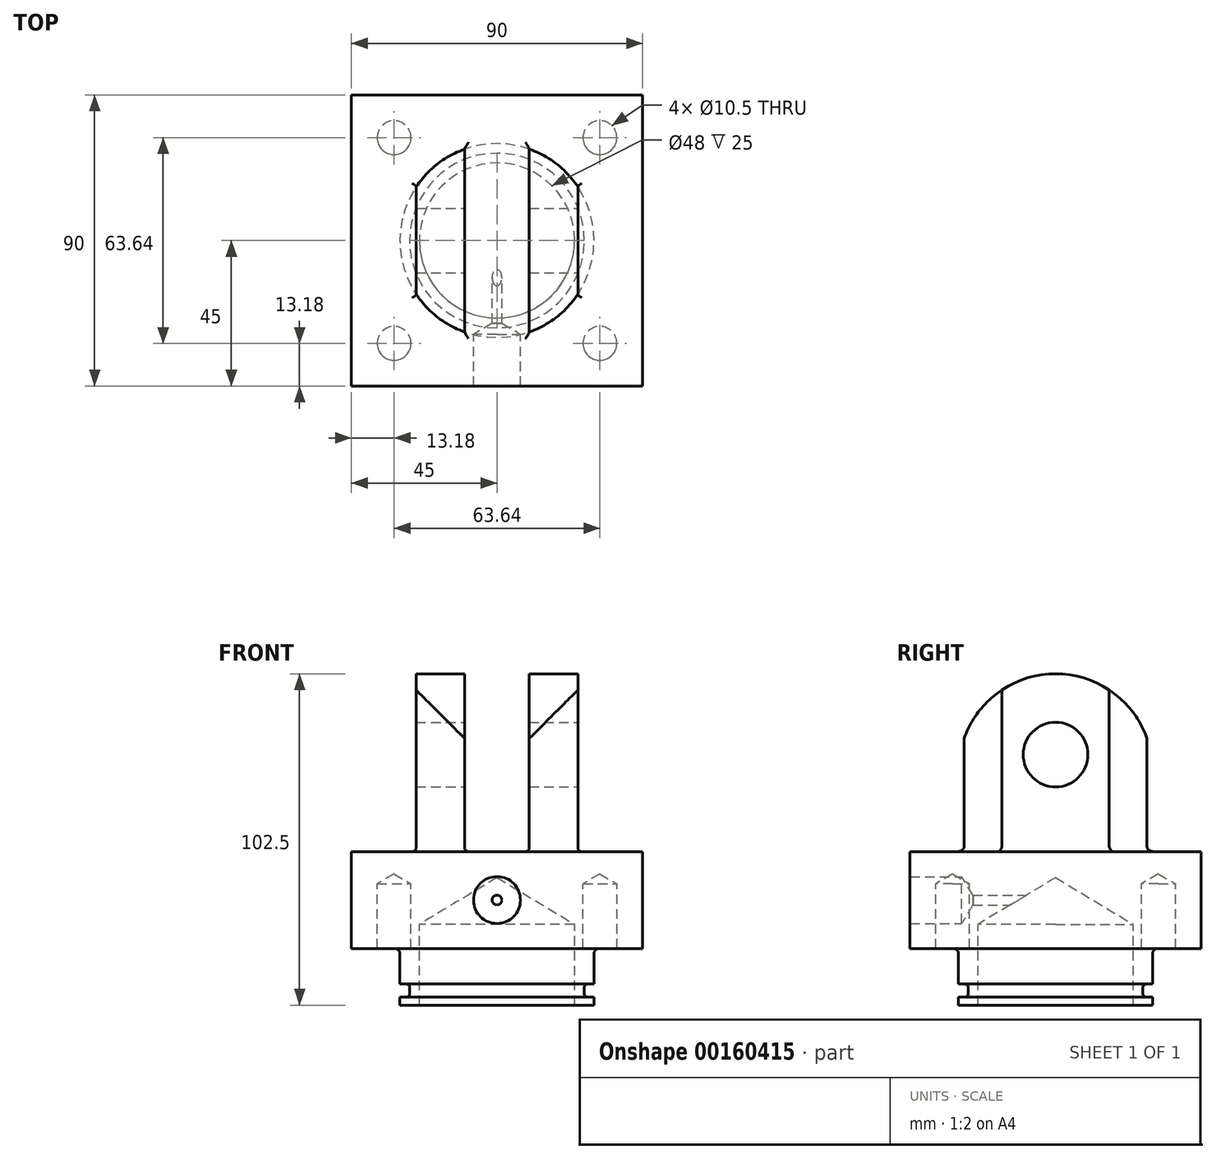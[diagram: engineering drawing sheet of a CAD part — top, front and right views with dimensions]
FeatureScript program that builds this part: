
annotation { "Feature Type Name" : "Feature", "Feature Type Description" : "" }
export const myFeature = defineFeature(function(context is Context, id is Id, definition is map)
    precondition{}
    {
        {
            var Q0;
            Q0=qCreatedBy(makeId("Top.planeOp"),FACE);
            var sketch = newSketch(context, id + "F0", { "sketchPlane" : qUnion([Q0])});
            skLineSegment(sketch, "E0.bottom", {"start": v(45, 45) * mm, "end": v(-45, 45) * mm});
            skLineSegment(sketch, "E0.top", {"start": v(45, -45) * mm, "end": v(-45, -45) * mm});
            skLineSegment(sketch, "E0.left", {"start": v(45, 45) * mm, "end": v(45, -45) * mm});
            skLineSegment(sketch, "E0.right", {"start": v(-45, 45) * mm, "end": v(-45, -45) * mm});
            skPoint(sketch, "E0.middle", {"position": v(0, 0) * mm});
            skSolve(sketch);
        }
        {
            var Q0;
            Q0 = qSketchRegion(id + "F0", true);
            extrude(context, id + "F1", {"entities" : qUnion([Q0]), "depth" : 102.5 * mm});
        }
        {
            var Q0;
            Q0=makeQuery(id+"F1.opExtrude","CAP_VERTEX",VERTEX,{"disambiguationData":[OSD([sQuery(id+"F0.wireOp",EDGE,"E0.top"),sQuery(id+"F0.wireOp",EDGE,"E0.right")])],"isStart":false});
            var Q1;
            Q1=makeQuery(id+"F1.opExtrude","CAP_VERTEX",VERTEX,{"disambiguationData":[OSD([sQuery(id+"F0.wireOp",EDGE,"E0.bottom"),sQuery(id+"F0.wireOp",EDGE,"E0.left")])],"isStart":false});
            var Q2;
            Q2=makeQuery(id+"F1.opExtrude","CAP_VERTEX",VERTEX,{"disambiguationData":[OSD([sQuery(id+"F0.wireOp",EDGE,"E0.bottom"),sQuery(id+"F0.wireOp",EDGE,"E0.left")])],"isStart":true});
            cPlane(context, id + "F2", {"entities" : qUnion([Q0, Q1, Q2]), "cplaneType" : CPlaneType.THREE_POINT, "offset" : 25 * mm, "width" : 150 * mm, "height" : 150 * mm});
        }
        {
            var Q0;
            Q0=qCreatedBy(id+"F2.planeOp",FACE);
            var sketch = newSketch(context, id + "F3", { "sketchPlane" : qUnion([Q0])});
            skLineSegment(sketch, "E1.bottom", {"start": v(-63.64, 102.5) * mm, "end": v(-30, 102.5) * mm});
            skLineSegment(sketch, "E1.top", {"start": v(-63.64, 47.5) * mm, "end": v(-31.6, 47.5) * mm});
            skLineSegment(sketch, "E1.left", {"start": v(-63.64, 102.5) * mm, "end": v(-63.64, 47.5) * mm});
            skLineSegment(sketch, "E1.right", {"start": v(-30, 102.5) * mm, "end": v(-30, 49.1) * mm});
            skLineSegment(sketch, "E2.bottom", {"start": v(-63.64, 0) * mm, "end": v(-30, 0) * mm});
            skLineSegment(sketch, "E2.top", {"start": v(-63.64, 17.5) * mm, "end": v(-31.6, 17.5) * mm});
            skLineSegment(sketch, "E2.left", {"start": v(-63.64, 0) * mm, "end": v(-63.64, 17.5) * mm});
            skLineSegment(sketch, "E2.right", {"start": v(-30, 0) * mm, "end": v(-30, 2.5) * mm});
            skLineSegment(sketch, "E3", {"start": v(0, -1.6) * mm, "end": v(0, 125.64) * mm, "construction": true});
            skLineSegment(sketch, "E4.bottom", {"start": v(-30, 2.5) * mm, "end": v(-28, 2.5) * mm});
            skLineSegment(sketch, "E4.top", {"start": v(-30, 6.5) * mm, "end": v(-28, 6.5) * mm});
            skLineSegment(sketch, "E4.right", {"start": v(-27, 3.5) * mm, "end": v(-27, 5.5) * mm});
            skLineSegment(sketch, "E5.trimOffspring", {"start": v(-30, 6.5) * mm, "end": v(-30, 15.9) * mm});
            skPoint(sketch, "E6.visualSharp", {"position": v(-30, 47.5) * mm});
            skArc(sketch, "E6.filletArc", {"start": v(-31.6, 47.5) * mm, "mid": v(-30.47, 47.97) * mm, "end": v(-30, 49.1) * mm});
            skPoint(sketch, "E7.visualSharp", {"position": v(-30, 17.5) * mm});
            skArc(sketch, "E7.filletArc", {"start": v(-30, 15.9) * mm, "mid": v(-30.47, 17.03) * mm, "end": v(-31.6, 17.5) * mm});
            skPoint(sketch, "E8.visualSharp", {"position": v(-27, 6.5) * mm});
            skArc(sketch, "E8.filletArc", {"start": v(-27, 5.5) * mm, "mid": v(-27.3, 6.2) * mm, "end": v(-28, 6.5) * mm});
            skPoint(sketch, "E9.visualSharp", {"position": v(-27, 2.5) * mm});
            skArc(sketch, "E9.filletArc", {"start": v(-28, 2.5) * mm, "mid": v(-27.3, 2.8) * mm, "end": v(-27, 3.5) * mm});
            skSolve(sketch);
        }
        {
            var Q0;
            Q0 = qSketchRegion(id + "F3", true);
            var Q1;
            Q1=sQuery(id+"F3.wireOp",EDGE,"E3");
            revolve(context, id + "F4", {"operationType" : NewBodyOperationType.REMOVE, "entities" : qUnion([Q0]), "axis" : qUnion([Q1]), "revolveType" : RevolveType.FULL, "oppositeDirection" : true});
        }
        {
            var Q0;
            Q0=makeQuery(id+"F1.opExtrude","CAP_FACE",FACE,{"disambiguationData":[OSD([sQuery(id+"F0.wireOp",EDGE,"E0.bottom"),sQuery(id+"F0.wireOp",EDGE,"E0.top"),sQuery(id+"F0.wireOp",EDGE,"E0.left"),sQuery(id+"F0.wireOp",EDGE,"E0.right")])],"isStart":true});
            var sketch = newSketch(context, id + "F5", { "sketchPlane" : qUnion([Q0])});
            skPoint(sketch, "E10", {"position": v(0, 0) * mm});
            skSolve(sketch);
        }
        {
            var Q0;
            Q0=sQuery(id+"F5.wireOp",VERTEX,"E10");
            var Q1;
            Q1=makeQuery(id+"F1.opExtrude","SWEPT_BODY",BODY,{"disambiguationData":[OSD([sQuery(id+"F0.wireOp",EDGE,"E0.bottom"),sQuery(id+"F0.wireOp",EDGE,"E0.top"),sQuery(id+"F0.wireOp",EDGE,"E0.left"),sQuery(id+"F0.wireOp",EDGE,"E0.right")])]});
            hole(context, id + "F6", {"style" : HoleStyle.SIMPLE, "endStyle" : HoleEndStyle.BLIND, "holeDiameter" : 48 * mm, "holeDepth" : 25 * mm, "locations" : qUnion([Q0]), "scope" : qUnion([Q1]), "startStyle" : HoleStartStyle.SKETCH});
        }
        {
            var Q0;
            Q0=qCreatedBy(makeId("Front.planeOp"),FACE);
            var sketch = newSketch(context, id + "F7", { "sketchPlane" : qUnion([Q0])});
            skLineSegment(sketch, "E11.bottom", {"start": v(-45, 47.5) * mm, "end": v(-26.2, 47.5) * mm});
            skLineSegment(sketch, "E11.top", {"start": v(-45, 102.5) * mm, "end": v(-25, 102.5) * mm});
            skLineSegment(sketch, "E11.left", {"start": v(-45, 47.5) * mm, "end": v(-45, 102.5) * mm});
            skLineSegment(sketch, "E11.right", {"start": v(-25, 48.7) * mm, "end": v(-25, 102.5) * mm});
            skLineSegment(sketch, "E12.bottom", {"start": v(8.8, 47.5) * mm, "end": v(-8.8, 47.5) * mm});
            skLineSegment(sketch, "E12.top", {"start": v(10, 102.5) * mm, "end": v(-10, 102.5) * mm});
            skLineSegment(sketch, "E12.left", {"start": v(10, 48.7) * mm, "end": v(10, 102.5) * mm});
            skLineSegment(sketch, "E12.right", {"start": v(-10, 48.7) * mm, "end": v(-10, 102.5) * mm});
            skLineSegment(sketch, "E13.bottom", {"start": v(45, 47.5) * mm, "end": v(26.2, 47.5) * mm});
            skLineSegment(sketch, "E13.top", {"start": v(45, 102.5) * mm, "end": v(25, 102.5) * mm});
            skLineSegment(sketch, "E13.left", {"start": v(45, 47.5) * mm, "end": v(45, 102.5) * mm});
            skLineSegment(sketch, "E13.right", {"start": v(25, 48.7) * mm, "end": v(25, 102.5) * mm});
            skLineSegment(sketch, "E14", {"start": v(0, -1.6) * mm, "end": v(0, 109.32) * mm, "construction": true});
            skPoint(sketch, "E15.visualSharp", {"position": v(-25, 47.5) * mm});
            skArc(sketch, "E15.filletArc", {"start": v(-26.2, 47.5) * mm, "mid": v(-25.35, 47.85) * mm, "end": v(-25, 48.7) * mm});
            skPoint(sketch, "E16.visualSharp", {"position": v(-10, 47.5) * mm});
            skArc(sketch, "E16.filletArc", {"start": v(-10, 48.7) * mm, "mid": v(-9.65, 47.85) * mm, "end": v(-8.8, 47.5) * mm});
            skPoint(sketch, "E17.visualSharp", {"position": v(10, 47.5) * mm});
            skArc(sketch, "E17.filletArc", {"start": v(8.8, 47.5) * mm, "mid": v(9.65, 47.85) * mm, "end": v(10, 48.7) * mm});
            skPoint(sketch, "E18.visualSharp", {"position": v(25, 47.5) * mm});
            skArc(sketch, "E18.filletArc", {"start": v(25, 48.7) * mm, "mid": v(25.35, 47.85) * mm, "end": v(26.2, 47.5) * mm});
            skSolve(sketch);
        }
        {
            var Q0;
            Q0 = qSketchRegion(id + "F7", true);
            extrude(context, id + "F8", {"entities" : qUnion([Q0]), "operationType" : NewBodyOperationType.REMOVE, "endBound" : BoundingType.THROUGH_ALL, "oppositeDirection" : true, "depth" : 25 * mm, "hasSecondDirection" : true, "secondDirectionBound" : BoundingType.THROUGH_ALL, "secondDirectionOppositeDirection" : false, "secondDirectionDepth" : 25 * mm});
        }
        {
            var Q0;
            Q0=qCreatedBy(makeId("Right.planeOp"),FACE);
            var sketch = newSketch(context, id + "F9", { "sketchPlane" : qUnion([Q0])});
            skArc(sketch, "E19", {"start": v(28.28, 82.5) * mm, "mid": v(0, 102.5) * mm, "end": v(-28.28, 82.5) * mm});
            skLineSegment(sketch, "E20", {"start": v(28.28, 82.5) * mm, "end": v(28.28, 102.5) * mm});
            skLineSegment(sketch, "E21", {"start": v(28.28, 102.5) * mm, "end": v(-28.28, 102.5) * mm});
            skLineSegment(sketch, "E22", {"start": v(-28.28, 102.5) * mm, "end": v(-28.28, 82.5) * mm});
            skCircle(sketch, "E23", {"center": v(0, 77.5) * mm, "radius": 10 * mm});
            skSolve(sketch);
        }
        {
            var Q0;
            Q0 = qSketchRegion(id + "F9", true);
            var Q1;
            Q1=makeQuery(id+"F8.boolean.opBoolean","COPY",FACE,{"derivedFrom":makeQuery(id+"F8.opExtrude","SWEPT_FACE",FACE,{"disambiguationData":[OSD([sQuery(id+"F7.wireOp",EDGE,"E11.right")])]})});
            var Q2;
            Q2=makeQuery(id+"F8.boolean.opBoolean","COPY",FACE,{"derivedFrom":makeQuery(id+"F8.opExtrude","SWEPT_FACE",FACE,{"disambiguationData":[OSD([sQuery(id+"F7.wireOp",EDGE,"E13.right")])]})});
            extrude(context, id + "F10", {"entities" : qUnion([Q0]), "operationType" : NewBodyOperationType.REMOVE, "endBound" : BoundingType.UP_TO_SURFACE, "oppositeDirection" : true, "endBoundEntityFace" : qUnion([Q1]), "depth" : 25 * mm, "hasSecondDirection" : true, "secondDirectionBound" : BoundingType.UP_TO_SURFACE, "secondDirectionOppositeDirection" : false, "secondDirectionBoundEntityFace" : qUnion([Q2]), "secondDirectionDepth" : 25 * mm});
        }
        {
            var Q0;
            Q0=makeQuery(id+"F4.boolean.opBoolean","COPY",FACE,{"derivedFrom":makeQuery(id+"F4.opRevolve","SWEPT_FACE",FACE,{"disambiguationData":[OSD([sQuery(id+"F3.wireOp",EDGE,"E2.top")])]})});
            var sketch = newSketch(context, id + "F11", { "sketchPlane" : qUnion([Q0])});
            skLineSegment(sketch, "E24", {"start": v(45, -45) * mm, "end": v(-45, 45) * mm, "construction": true});
            skLineSegment(sketch, "E25", {"start": v(45, 45) * mm, "end": v(-45, -45) * mm, "construction": true});
            skCircle(sketch, "E26", {"center": v(0, 0) * mm, "radius": 45 * mm, "construction": true});
            skPoint(sketch, "E27", {"position": v(-31.82, -31.82) * mm});
            skPoint(sketch, "E28", {"position": v(-31.82, 31.82) * mm});
            skPoint(sketch, "E29", {"position": v(31.82, 31.82) * mm});
            skPoint(sketch, "E30", {"position": v(31.82, -31.82) * mm});
            skSolve(sketch);
        }
        {
            var Q0;
            Q0=sQuery(id+"F11.wireOp",VERTEX,"E27");
            var Q1;
            Q1=sQuery(id+"F11.wireOp",VERTEX,"E28");
            var Q2;
            Q2=sQuery(id+"F11.wireOp",VERTEX,"E29");
            var Q3;
            Q3=sQuery(id+"F11.wireOp",VERTEX,"E30");
            var Q4;
            Q4=makeQuery(id+"F1.opExtrude","SWEPT_BODY",BODY,{"disambiguationData":[OSD([sQuery(id+"F0.wireOp",EDGE,"E0.bottom"),sQuery(id+"F0.wireOp",EDGE,"E0.top"),sQuery(id+"F0.wireOp",EDGE,"E0.left"),sQuery(id+"F0.wireOp",EDGE,"E0.right")])]});
            hole(context, id + "F12", {"style" : HoleStyle.SIMPLE, "endStyle" : HoleEndStyle.BLIND, "standardTappedOrClearance" : lookupTablePath({ "standard" : "ISO", "engagement" : "75%", "pitch" : "1.5 mm", "size" : "M12", "type" : "Tapped" }), "standardBlindInLast" : lookupTablePath({ "standard" : "ISO", "engagement" : "75%", "pitch" : "1.5 mm", "size" : "M12", "type" : "Tapped" }), "holeDiameter" : 10.5 * mm, "holeDepth" : 20 * mm, "locations" : qUnion([Q0, Q1, Q2, Q3]), "scope" : qUnion([Q4]), "tappedDepth" : 12 * mm, "tapClearance" : 3, "majorDiameter" : 12 * mm, "startStyle" : HoleStartStyle.SKETCH});
        }
        {
            var Q0;
            Q0=makeQuery(id+"F1.opExtrude","SWEPT_FACE",FACE,{"disambiguationData":[OSD([sQuery(id+"F0.wireOp",EDGE,"E0.top")])]});
            var sketch = newSketch(context, id + "F13", { "sketchPlane" : qUnion([Q0])});
            skPoint(sketch, "E31", {"position": v(0, 32.5) * mm});
            skSolve(sketch);
        }
        {
            var Q0;
            Q0=sQuery(id+"F13.wireOp",VERTEX,"E31");
            var Q1;
            Q1=makeQuery(id+"F1.opExtrude","SWEPT_BODY",BODY,{"disambiguationData":[OSD([sQuery(id+"F0.wireOp",EDGE,"E0.bottom"),sQuery(id+"F0.wireOp",EDGE,"E0.top"),sQuery(id+"F0.wireOp",EDGE,"E0.left"),sQuery(id+"F0.wireOp",EDGE,"E0.right")])]});
            hole(context, id + "F14", {"style" : HoleStyle.SIMPLE, "endStyle" : HoleEndStyle.BLIND, "holeDiameter" : 3 * mm, "holeDepth" : 45 * mm, "locations" : qUnion([Q0]), "scope" : qUnion([Q1]), "startStyle" : HoleStartStyle.SKETCH});
        }
        {
            var Q0;
            Q0=sQuery(id+"F13.wireOp",VERTEX,"E31");
            var Q1;
            Q1=makeQuery(id+"F1.opExtrude","SWEPT_BODY",BODY,{"disambiguationData":[OSD([sQuery(id+"F0.wireOp",EDGE,"E0.bottom"),sQuery(id+"F0.wireOp",EDGE,"E0.top"),sQuery(id+"F0.wireOp",EDGE,"E0.left"),sQuery(id+"F0.wireOp",EDGE,"E0.right")])]});
            hole(context, id + "F15", {"style" : HoleStyle.SIMPLE, "endStyle" : HoleEndStyle.BLIND, "standardTappedOrClearance" : lookupTablePath({ "standard" : "ISO", "engagement" : "75%", "pitch" : "1.5 mm", "size" : "M16", "type" : "Tapped" }), "standardBlindInLast" : lookupTablePath({ "standard" : "ISO", "engagement" : "75%", "pitch" : "1.5 mm", "size" : "M16", "type" : "Tapped" }), "holeDiameter" : 14.5 * mm, "holeDepth" : 16 * mm, "locations" : qUnion([Q0]), "scope" : qUnion([Q1]), "majorDiameter" : 16 * mm, "startStyle" : HoleStartStyle.SKETCH});
        }
    });
